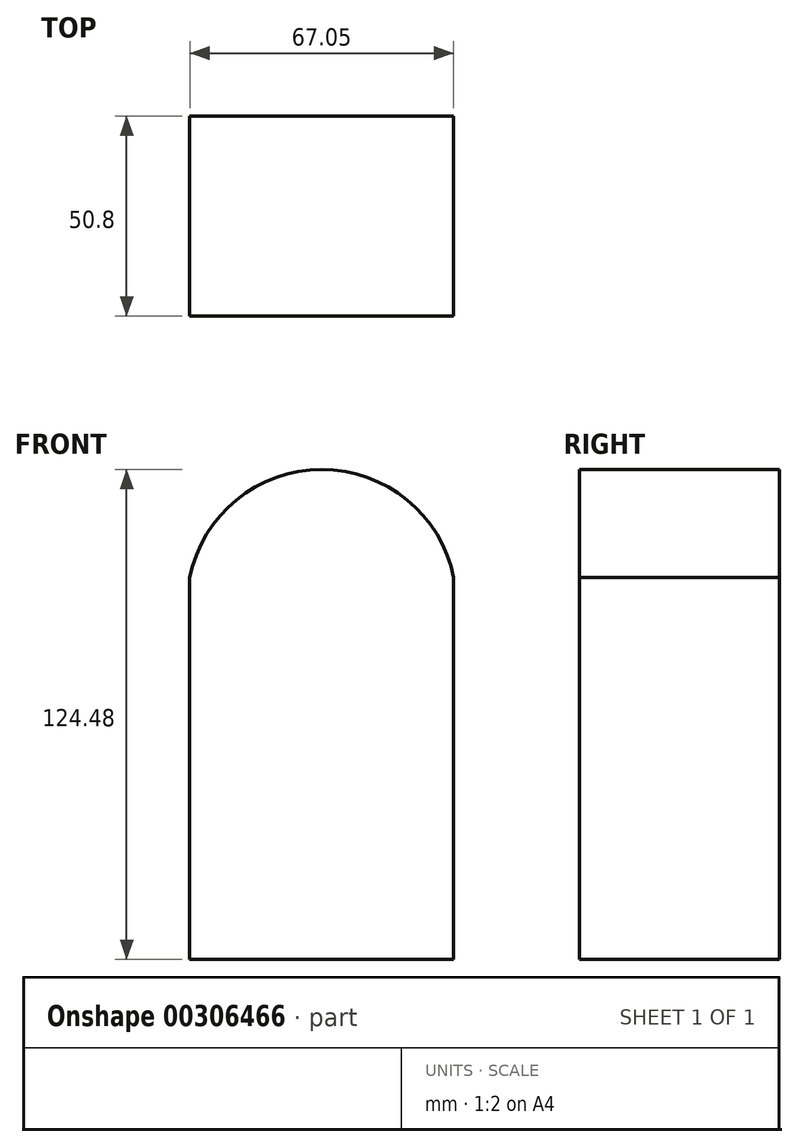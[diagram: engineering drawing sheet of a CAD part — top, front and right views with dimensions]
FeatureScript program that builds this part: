
annotation { "Feature Type Name" : "Feature", "Feature Type Description" : "" }
export const myFeature = defineFeature(function(context is Context, id is Id, definition is map)
    precondition{}
    {
        {
            var Q0;
            Q0=qCreatedBy(makeId("Front.planeOp"),FACE);
            var sketch = newSketch(context, id + "F0", { "sketchPlane" : qUnion([Q0])});
            skLineSegment(sketch, "E0.bottom", {"start": v(-45.97, 44.96) * mm, "end": v(21.08, 44.96) * mm});
            skLineSegment(sketch, "E0.top", {"start": v(-45.97, -52.07) * mm, "end": v(21.08, -52.07) * mm});
            skLineSegment(sketch, "E0.left", {"start": v(-45.97, 44.96) * mm, "end": v(-45.97, -52.07) * mm});
            skLineSegment(sketch, "E0.right", {"start": v(21.08, 44.96) * mm, "end": v(21.08, -52.07) * mm});
            skArc(sketch, "E1", {"start": v(21.08, 44.96) * mm, "mid": v(-12.45, 72.4) * mm, "end": v(-45.97, 44.96) * mm});
            skSolve(sketch);
        }
        {
            var Q0;
            Q0=makeQuery(id+"F0.imprint","IMPRINT",FACE,{"disambiguationData":[TD([[makeQuery(id+"F0.imprint","IMPRINT",EDGE,{"derivedFrom":sQuery(id+"F0.wireOp",EDGE,"E0.bottom")}),1.0]])]});
            var Q1;
            Q1=makeQuery(id+"F0.imprint","IMPRINT",FACE,{"disambiguationData":[TD([[makeQuery(id+"F0.imprint","IMPRINT",EDGE,{"derivedFrom":sQuery(id+"F0.wireOp",EDGE,"E0.bottom")}),-1.0]])]});
            extrude(context, id + "F1", {"entities" : qUnion([Q0, Q1]), "depth" : 50.8 * mm});
        }
    });
